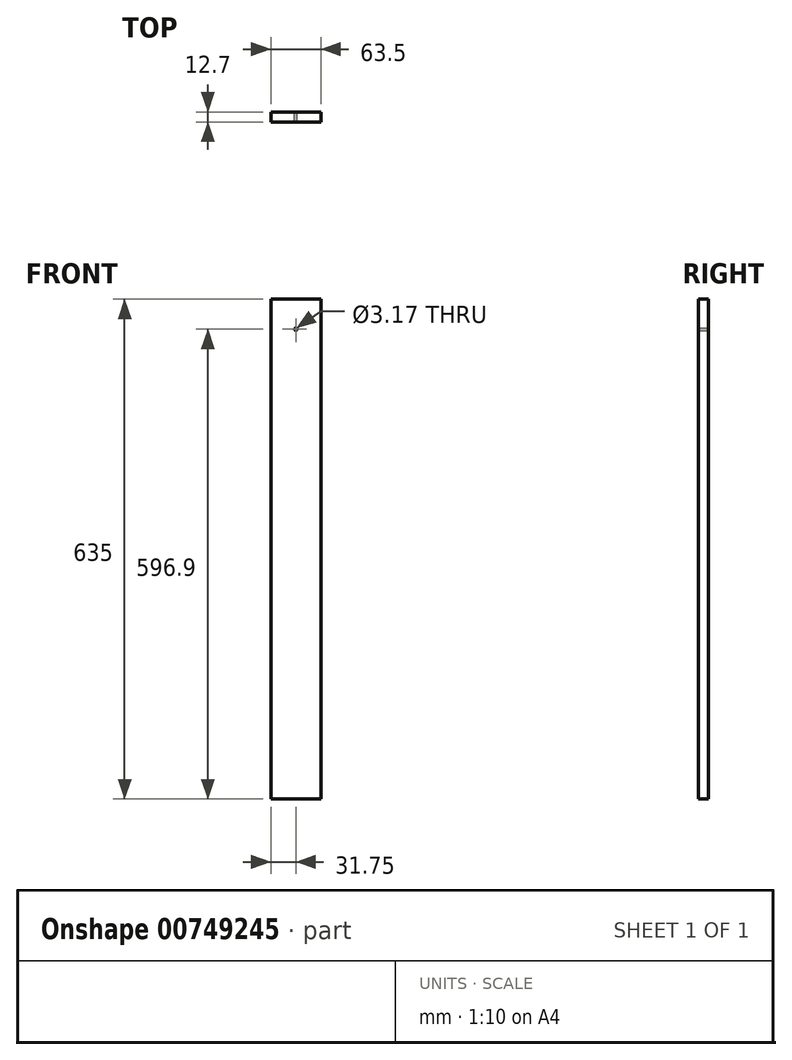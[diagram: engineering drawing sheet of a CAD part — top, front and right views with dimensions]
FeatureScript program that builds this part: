
annotation { "Feature Type Name" : "Feature", "Feature Type Description" : "" }
export const myFeature = defineFeature(function(context is Context, id is Id, definition is map)
    precondition{}
    {
        {
            var Q0;
            Q0=qCreatedBy(makeId("Top.planeOp"),FACE);
            var sketch = newSketch(context, id + "F0", { "sketchPlane" : qUnion([Q0])});
            skLineSegment(sketch, "E0.bottom", {"start": v(31.75, 6.35) * mm, "end": v(-31.75, 6.35) * mm});
            skLineSegment(sketch, "E0.top", {"start": v(31.75, -6.35) * mm, "end": v(-31.75, -6.35) * mm});
            skLineSegment(sketch, "E0.left", {"start": v(31.75, 6.35) * mm, "end": v(31.75, -6.35) * mm});
            skLineSegment(sketch, "E0.right", {"start": v(-31.75, 6.35) * mm, "end": v(-31.75, -6.35) * mm});
            skPoint(sketch, "E0.middle", {"position": v(0, 0) * mm});
            skSolve(sketch);
        }
        {
            var Q0;
            Q0 = qSketchRegion(id + "F0", true);
            extrude(context, id + "F1", {"entities" : qUnion([Q0]), "depth" : 635 * mm, "offsetDistance" : 25.4 * mm});
        }
        {
            var Q0;
            Q0=makeQuery(id+"F1.opExtrude","SWEPT_FACE",FACE,{"disambiguationData":[OSD([sQuery(id+"F0.wireOp",EDGE,"E0.bottom")])]});
            var sketch = newSketch(context, id + "F2", { "sketchPlane" : qUnion([Q0])});
            skLineSegment(sketch, "E1", {"start": v(0, 635) * mm, "end": v(0, 284.5) * mm, "construction": true});
            skCircle(sketch, "E2", {"center": v(0, 596.9) * mm, "radius": 1.59 * mm});
            skSolve(sketch);
        }
        {
            var Q0;
            Q0 = qSketchRegion(id + "F2", true);
            extrude(context, id + "F3", {"entities" : qUnion([Q0]), "operationType" : NewBodyOperationType.REMOVE, "endBound" : BoundingType.THROUGH_ALL, "oppositeDirection" : true, "depth" : 25.4 * mm, "offsetDistance" : 25.4 * mm});
        }
    });
